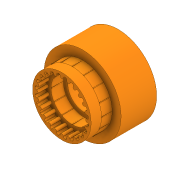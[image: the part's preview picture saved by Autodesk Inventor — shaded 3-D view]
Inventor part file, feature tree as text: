
AUTODESK INVENTOR PART (.ipt)
format: ipt  version: 2020 (Build 240168000, 168)  size: 636,928 bytes
history: native  units: in
note: dims shown in document units (in); Inventor stores cm internally (conversion verified against a paired STEP export)
features: sketch x7, extrude x6, chamfer x2, plane x1, projected_geometry x1
ambient origin geometry x8: Origin, YZ Plane, XZ Plane, XY Plane, X Axis, Y Axis, Z Axis, Center Point
bodies: Solid1 (feature_tree)
feature tree (17):
  extrude  "Extrusion1"  Depth=2.0472in
  extrude  "Extrusion2"  Depth=1.1024in
  chamfer  "Chamfer2"  Distance=0.2756in
  extrude  "Extrusion4"  Depth=0.2756in
  extrude  "Extrusion7"  Depth=0.2756in TaperAngle=0.0deg
  chamfer  "Chamfer4"  Distance=0.0394in
  extrude  "Extrusion8"  Depth=0.2756in
  sketch  "Sketch12"  dims[d39=1.4567in d57=0.0394in d58=0.0in]
  plane  "Work Plane1"
  sketch  "Sketch13"  dims[d59=0.315in d60=0.125in d61=0.0137in d67=0.0157in d68=4.7244in d70=360.0deg d72=0.0394in d73=0.0in d83=0.0591in d84=0.0866in d85=0.0827in d86=0.0827in d87=0.0827in d88=9.4488in d90=360.0deg d92=0.2756in d94=9.4488in d95=0.0827in d96=0.0827in d97=0.0827in d98=360.0deg d105=0.2756in d106=0.0in]
  extrude  "Extrusion10"  Depth=0.2756in TaperAngle=360.0deg
  sketch  "Sketch1"  dims[d0=0.8661in d1=2.0472in]
  sketch  "Sketch2"  dims[d2=0.9449in d3=0.0in d4=1.1024in]
  sketch  "Sketch4"  dims[d5=1.5748in d6=0.2756in d7=0.0in]
  sketch  "Sketch8"  dims[d11=0.2756in d12=0.125in d13=0.0137in d25=0.0157in]
  projected_geometry  "Projected Loop2"
  sketch  "Sketch10"  dims[d26=6.2992in d28=360.0deg d30=0.2756in d31=0.0in]
